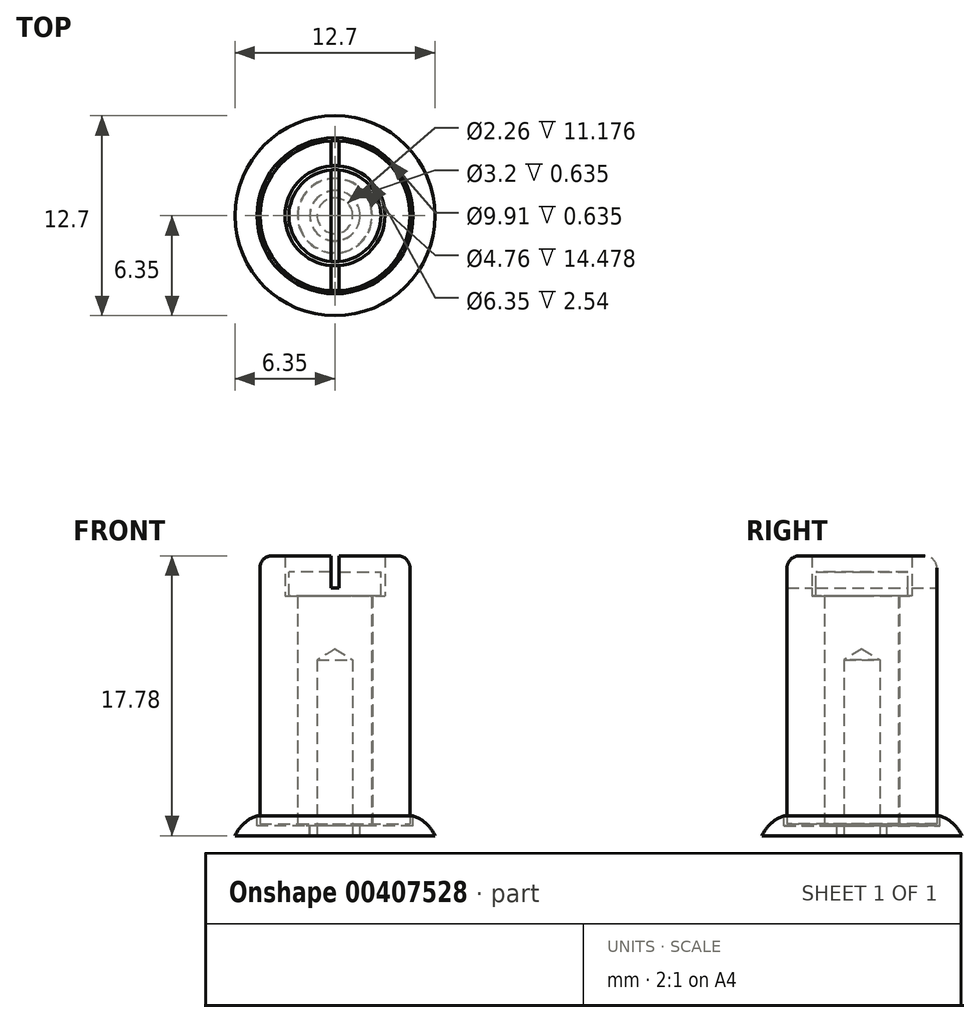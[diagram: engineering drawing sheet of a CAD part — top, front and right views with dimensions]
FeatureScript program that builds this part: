
annotation { "Feature Type Name" : "Feature", "Feature Type Description" : "" }
export const myFeature = defineFeature(function(context is Context, id is Id, definition is map)
    precondition{}
    {
        {
            var Q0;
            Q0=qCreatedBy(makeId("Front.planeOp"),FACE);
            var sketch = newSketch(context, id + "F0", { "sketchPlane" : qUnion([Q0])});
            skLineSegment(sketch, "E0", {"start": v(2.38, 0.76) * mm, "end": v(2.38, 15.24) * mm});
            skLineSegment(sketch, "E1", {"start": v(2.38, 15.24) * mm, "end": v(3.17, 15.24) * mm});
            skLineSegment(sketch, "E2", {"start": v(3.17, 15.24) * mm, "end": v(3.17, 17.78) * mm});
            skLineSegment(sketch, "E3", {"start": v(3.17, 17.78) * mm, "end": v(4.76, 17.78) * mm});
            skLineSegment(sketch, "E4", {"start": v(4.76, 17.78) * mm, "end": v(4.76, 0.76) * mm});
            skLineSegment(sketch, "E5", {"start": v(4.76, 0.76) * mm, "end": v(2.38, 0.76) * mm});
            skLineSegment(sketch, "E6", {"start": v(0, 0) * mm, "end": v(0, 19.75) * mm, "construction": true});
            skSolve(sketch);
        }
        {
            var Q0;
            Q0 = qSketchRegion(id + "F0", true);
            var Q1;
            Q1=sQuery(id+"F0.wireOp",EDGE,"E6");
            revolve(context, id + "F1", {"entities" : qUnion([Q0]), "axis" : qUnion([Q1]), "revolveType" : RevolveType.FULL});
        }
        {
            var Q0;
            Q0=qCreatedBy(makeId("Front.planeOp"),FACE);
            var sketch = newSketch(context, id + "F2", { "sketchPlane" : qUnion([Q0])});
            skLineSegment(sketch, "E7", {"start": v(0, 0) * mm, "end": v(1.59, 0) * mm});
            skLineSegment(sketch, "E8", {"start": v(1.59, 0) * mm, "end": v(1.59, 0.64) * mm});
            skLineSegment(sketch, "E9", {"start": v(1.59, 0.64) * mm, "end": v(2.35, 0.64) * mm});
            skLineSegment(sketch, "E10", {"start": v(2.35, 0.64) * mm, "end": v(2.35, 15.24) * mm});
            skLineSegment(sketch, "E11", {"start": v(2.35, 15.24) * mm, "end": v(2.92, 15.24) * mm});
            skLineSegment(sketch, "E12", {"start": v(2.92, 15.24) * mm, "end": v(2.92, 16.76) * mm});
            skLineSegment(sketch, "E13", {"start": v(2.92, 16.76) * mm, "end": v(0, 16.76) * mm});
            skLineSegment(sketch, "E14", {"start": v(0, 16.76) * mm, "end": v(0, 0) * mm});
            skSolve(sketch);
        }
        {
            var Q0;
            Q0 = qSketchRegion(id + "F2", true);
            var Q1;
            Q1=sQuery(id+"F2.wireOp",EDGE,"E14");
            revolve(context, id + "F3", {"entities" : qUnion([Q0]), "axis" : qUnion([Q1]), "revolveType" : RevolveType.FULL});
        }
        {
            var Q0;
            Q0=qCreatedBy(makeId("Front.planeOp"),FACE);
            var sketch = newSketch(context, id + "F4", { "sketchPlane" : qUnion([Q0])});
            skLineSegment(sketch, "E15.bottom", {"start": v(0.25, 17.78) * mm, "end": v(-0.25, 17.78) * mm});
            skLineSegment(sketch, "E15.top", {"start": v(0.25, 15.75) * mm, "end": v(-0.25, 15.75) * mm});
            skLineSegment(sketch, "E15.left", {"start": v(0.25, 17.78) * mm, "end": v(0.25, 15.75) * mm});
            skLineSegment(sketch, "E15.right", {"start": v(-0.25, 17.78) * mm, "end": v(-0.25, 15.75) * mm});
            skPoint(sketch, "E15.middle", {"position": v(0, 16.76) * mm});
            skSolve(sketch);
        }
        {
            var Q0;
            Q0 = qSketchRegion(id + "F4", true);
            extrude(context, id + "F5", {"entities" : qUnion([Q0]), "operationType" : NewBodyOperationType.REMOVE, "endBound" : BoundingType.SYMMETRIC, "depth" : 25.4 * mm, "offsetDistance" : 25.4 * mm});
        }
        {
            var Q0;
            Q0=makeQuery(id+"F3.opRevolve","SWEPT_FACE",FACE,{"disambiguationData":[OSD([sQuery(id+"F2.wireOp",EDGE,"E7")])]});
            var sketch = newSketch(context, id + "F6", { "sketchPlane" : qUnion([Q0])});
            skPoint(sketch, "E16", {"position": v(0, 0) * mm});
            skSolve(sketch);
        }
        {
            var Q0;
            Q0=sQuery(id+"F6.wireOp",VERTEX,"E16");
            var Q1;
            Q1=makeQuery(id+"F3.opRevolve","SWEPT_BODY",BODY,{"disambiguationData":[OSD([sQuery(id+"F2.wireOp",EDGE,"E7"),sQuery(id+"F2.wireOp",EDGE,"E8"),sQuery(id+"F2.wireOp",EDGE,"E9"),sQuery(id+"F2.wireOp",EDGE,"E10"),sQuery(id+"F2.wireOp",EDGE,"E11"),sQuery(id+"F2.wireOp",EDGE,"E12"),sQuery(id+"F2.wireOp",EDGE,"E13"),sQuery(id+"F2.wireOp",EDGE,"E14")])]});
            hole(context, id + "F7", {"style" : HoleStyle.SIMPLE, "endStyle" : HoleEndStyle.BLIND, "standardTappedOrClearance" : lookupTablePath({ "standard" : "ANSI", "engagement" : "75%", "pitch" : "40 tpi", "size" : "#4", "type" : "Tapped" }), "standardBlindInLast" : lookupTablePath({ "standard" : "ANSI", "engagement" : "75%", "pitch" : "40 tpi", "size" : "#4", "type" : "Tapped" }), "holeDiameter" : 2.26 * mm, "majorDiameter" : 2.84 * mm, "showTappedDepth" : true, "holeDepth" : 11.18 * mm, "tappedDepth" : 9.27 * mm, "tapClearance" : 3, "locations" : qUnion([Q0]), "scope" : qUnion([Q1])});
        }
        {
            var Q0;
            Q0=makeQuery(id+"F1.opRevolve","SWEPT_EDGE",EDGE,{"disambiguationData":[OSD([sQuery(id+"F0.wireOp",EDGE,"E3"),sQuery(id+"F0.wireOp",EDGE,"E4")])]});
            fillet(context, id + "F8", {"entities" : qUnion([Q0]), "radius" : 0.76 * mm, "tangentPropagation" : true, "allowEdgeOverflow" : false});
        }
        {
            var Q0;
            Q0=qCreatedBy(makeId("Right.planeOp"),FACE);
            var sketch = newSketch(context, id + "F9", { "sketchPlane" : qUnion([Q0])});
            skLineSegment(sketch, "E17", {"start": v(1.6, 0.63) * mm, "end": v(1.6, 0) * mm});
            skLineSegment(sketch, "E18", {"start": v(1.6, 0) * mm, "end": v(6.35, 0) * mm});
            skLineSegment(sketch, "E19", {"start": v(1.6, 0.63) * mm, "end": v(4.95, 0.64) * mm});
            skLineSegment(sketch, "E20", {"start": v(4.95, 0.64) * mm, "end": v(4.95, 1.27) * mm});
            skArc(sketch, "E21", {"start": v(6.35, 0) * mm, "mid": v(5.78, 0.78) * mm, "end": v(4.95, 1.27) * mm});
            skLineSegment(sketch, "E22", {"start": v(0, 0) * mm, "end": v(0, -3.57) * mm, "construction": true});
            skSolve(sketch);
        }
        {
            var Q0;
            Q0=makeQuery(id+"F9.imprint","IMPRINT",FACE,{"disambiguationData":[TD([[makeQuery(id+"F9.imprint","IMPRINT",EDGE,{"derivedFrom":sQuery(id+"F9.wireOp",EDGE,"E17")}),1.0]])]});
            var Q1;
            Q1=sQuery(id+"F9.wireOp",EDGE,"E22");
            revolve(context, id + "F10", {"operationType" : NewBodyOperationType.ADD, "entities" : qUnion([Q0]), "axis" : qUnion([Q1]), "revolveType" : RevolveType.FULL});
        }
    });
